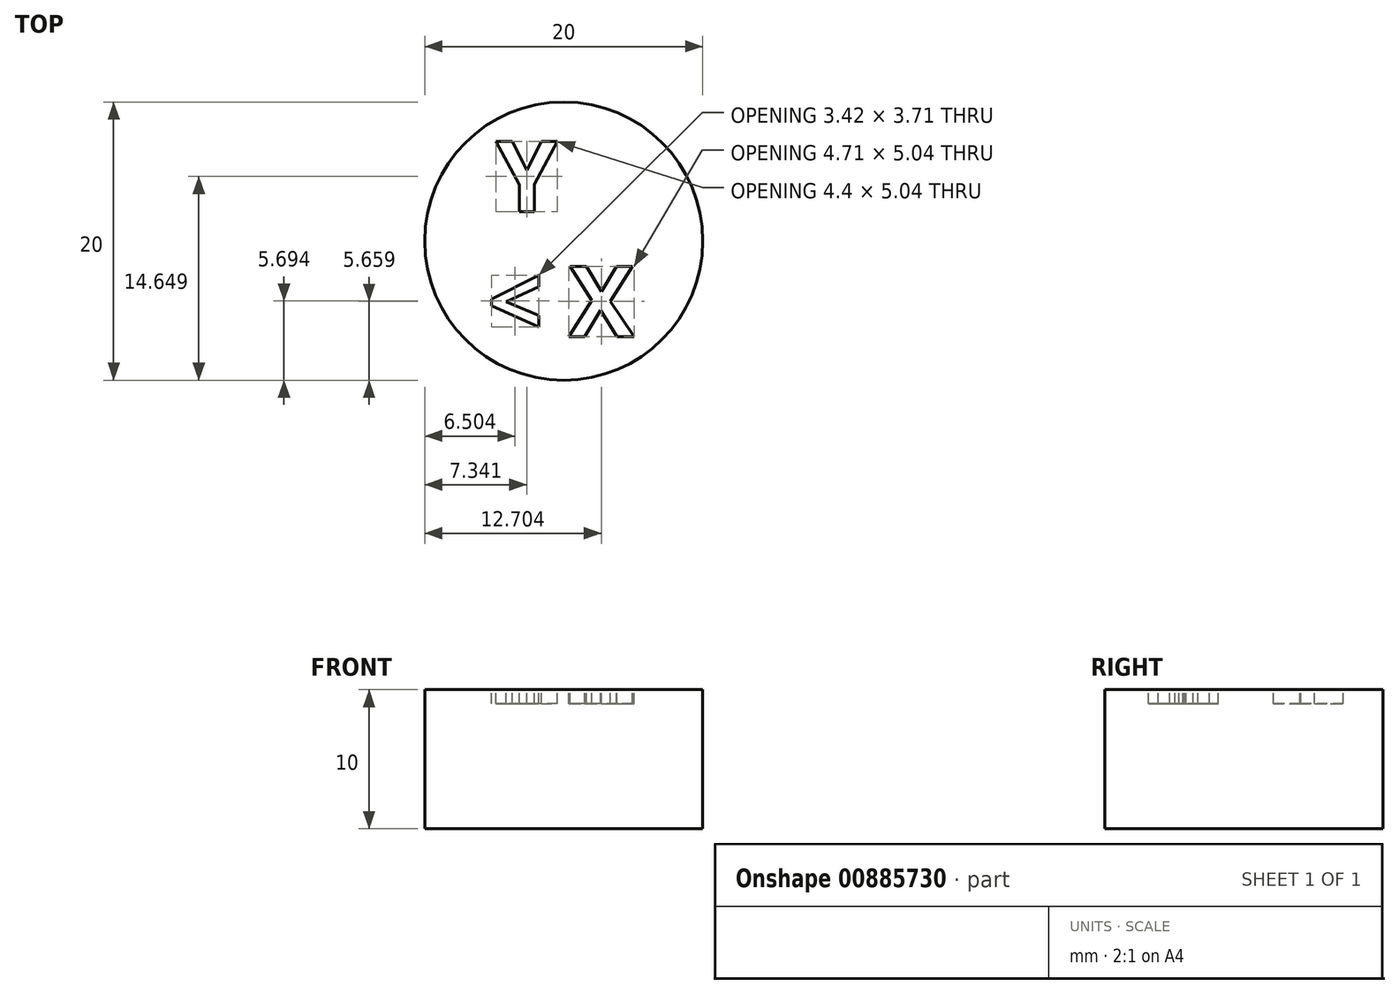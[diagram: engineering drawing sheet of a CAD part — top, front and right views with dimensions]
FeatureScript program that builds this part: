
annotation { "Feature Type Name" : "Feature", "Feature Type Description" : "" }
export const myFeature = defineFeature(function(context is Context, id is Id, definition is map)
    precondition{}
    {
        {
            var Q0;
            Q0=qCreatedBy(makeId("Top.planeOp"),FACE);
            var sketch = newSketch(context, id + "F0", { "sketchPlane" : qUnion([Q0])});
            skCircle(sketch, "E0", {"center": v(0, 0) * mm, "radius": 10 * mm});
            skSolve(sketch);
        }
        {
            var Q0;
            Q0 = qSketchRegion(id + "F0", true);
            extrude(context, id + "F1", {"entities" : qUnion([Q0]), "depth" : 10 * mm, "offsetDistance" : 25.4 * mm});
        }
        {
            var Q0;
            Q0=makeQuery(id+"F1.opExtrude","CAP_FACE",FACE,{"disambiguationData":[OSD([sQuery(id+"F0.wireOp",EDGE,"E0")])],"isStart":false});
            var sketch = newSketch(context, id + "F2", { "sketchPlane" : qUnion([Q0])});
            skText(sketch, "E1", { "text": "< X", "fontName": "OpenSans-Bold.ttf"});
            skText(sketch, "E2", { "text": "Y", "fontName": "OpenSans-Bold.ttf"});
            const initialGuessF2  = {"E1": [-0.00551, -0.00686, 1, 0, 0.00508], "E2": [-0.00486, 0.00213, 1, 0, 0.00508]};
            skSetInitialGuess(sketch, initialGuessF2);
            skSolve(sketch);
        }
        {
            var Q0;
            Q0 = qSketchRegion(id + "F2", true);
            extrude(context, id + "F3", {"entities" : qUnion([Q0]), "operationType" : NewBodyOperationType.REMOVE, "oppositeDirection" : true, "depth" : 1 * mm, "offsetDistance" : 25.4 * mm});
        }
    });
